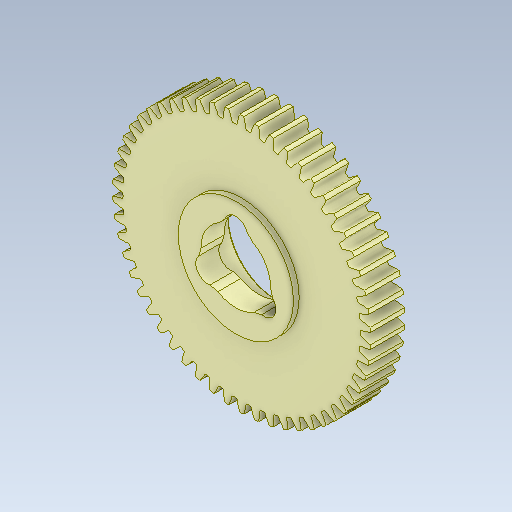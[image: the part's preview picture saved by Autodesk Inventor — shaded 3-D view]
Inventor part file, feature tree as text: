
AUTODESK INVENTOR PART (.ipt)
format: ipt  version: 2020 (Build 240168000, 168)  size: 792,576 bytes
history: native  units: in
note: dims shown in document units (in); Inventor stores cm internally (conversion verified against a paired STEP export)
features: chamfer x1
ambient origin geometry x8: Origin, YZ Plane, XZ Plane, XY Plane, X Axis, Y Axis, Z Axis, Center Point
bodies: Solid1 (feature_tree)
feature tree (1):
  chamfer  "Chamfer1"  [1 undecoded]
note: 1 required parameter value undecoded (feature->parameter linkage not recoverable at this tier; creation-order binding heuristic only, values carry confidence <= 0.55)
